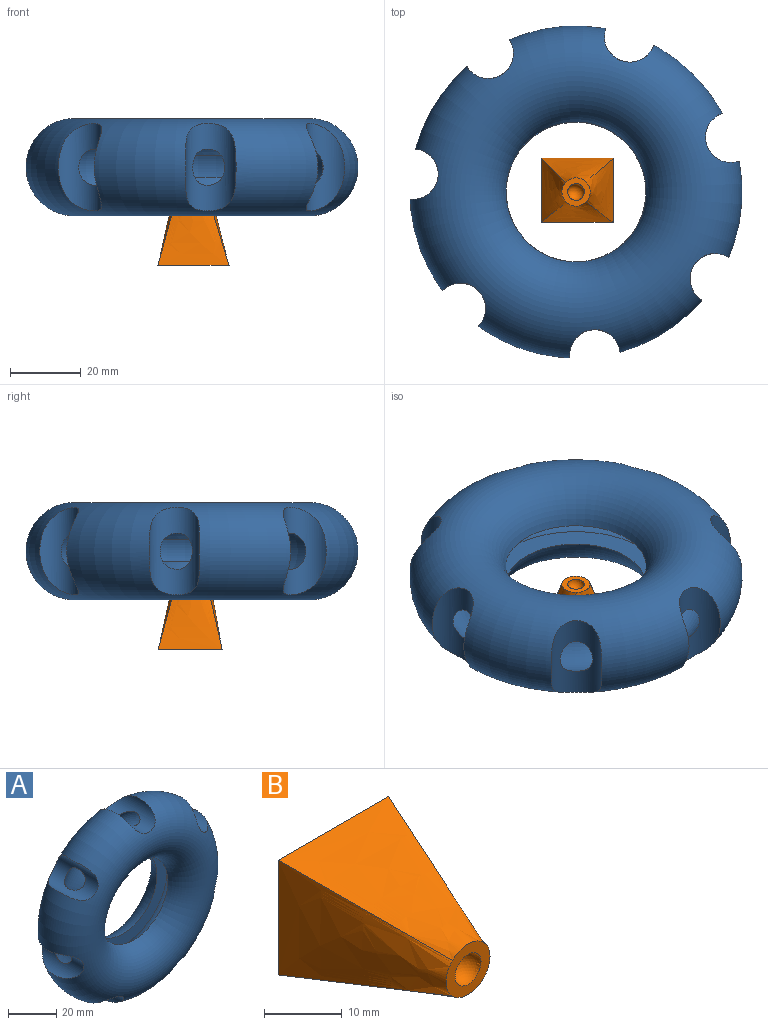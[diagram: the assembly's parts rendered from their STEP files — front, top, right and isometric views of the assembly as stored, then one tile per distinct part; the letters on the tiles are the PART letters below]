
ASSEMBLY  parts=2 mates=1
PART A: 11 faces, bbox 101.8x27.6x101.8 mm
  f0: torus R=33.23mm, axis (0,-1,0), area 8819.4mm2, adj f2,f3,f4,f5,f6,f7,f8,f9
  f1: torus R=33.23mm, axis (0,-1,0), area 14652.5mm2, adj f2,f3,f4,f5,f6,f7,f8,f9
  f2: plane 52.14x52.14mm, normal (0,1,0), area 893.1mm2, adj f0,f1
  f3: plane 51.63x51.63mm, normal (0,-1,0), area 868.4mm2, adj f0,f1
  f4: cylinder r=7.14mm len=24.76mm, axis (0,1,0), area 361.4mm2, adj f0,f1
  f5: cylinder r=7.14mm len=24.76mm, axis (0,1,0), area 361.6mm2, adj f0,f1
  f6: cylinder r=7.14mm len=24.76mm, axis (0,1,0), area 361.4mm2, adj f0,f1
  f7: cylinder r=7.14mm len=24.76mm, axis (0,1,0), area 361.4mm2, adj f0,f1
  f8: cylinder r=7.14mm len=24.76mm, axis (0,1,0), area 361.6mm2, adj f0,f1
  f9: cylinder r=7.14mm len=24.76mm, axis (0,1,0), area 361.2mm2, adj f0,f1
  f10: cylinder r=7.14mm len=24.76mm, axis (0,1,0), area 361.5mm2, adj f0,f1
PART B: 7 faces, bbox 20.1x25x18.1 mm
  f0: plane 8x8mm, normal (0,-1,0), area 32.7mm2, adj f2,f3,f4,f5,f6
  f1: plane 20.14x18.13mm, normal (0,1,0), area 365.1mm2, adj f2,f3,f4,f5
  f2: bspline ~25x20.14mm, area 336.4mm2, adj f0,f1,f3,f5
  f3: bspline ~25x18.13mm, area 313.2mm2, adj f0,f1,f2,f4
  f4: bspline ~25x20.14mm, area 333.5mm2, adj f0,f1,f3,f5
  f5: bspline ~25x18.13mm, area 310.7mm2, adj f0,f1,f2,f4
  f6: sphere r=2.37mm, area 35.2mm2, adj f0
PLACE A rot(axis=(-0.28,-0.68,0.68),148.7deg) t=(0,0,-30.71)mm
PLACE B rot(axis=(-1,0,0),90deg) t=(0,0,0)mm
MATE revolute B.f0 <-> A.f0  axis (0,0,1) through (0,0,0)mm
